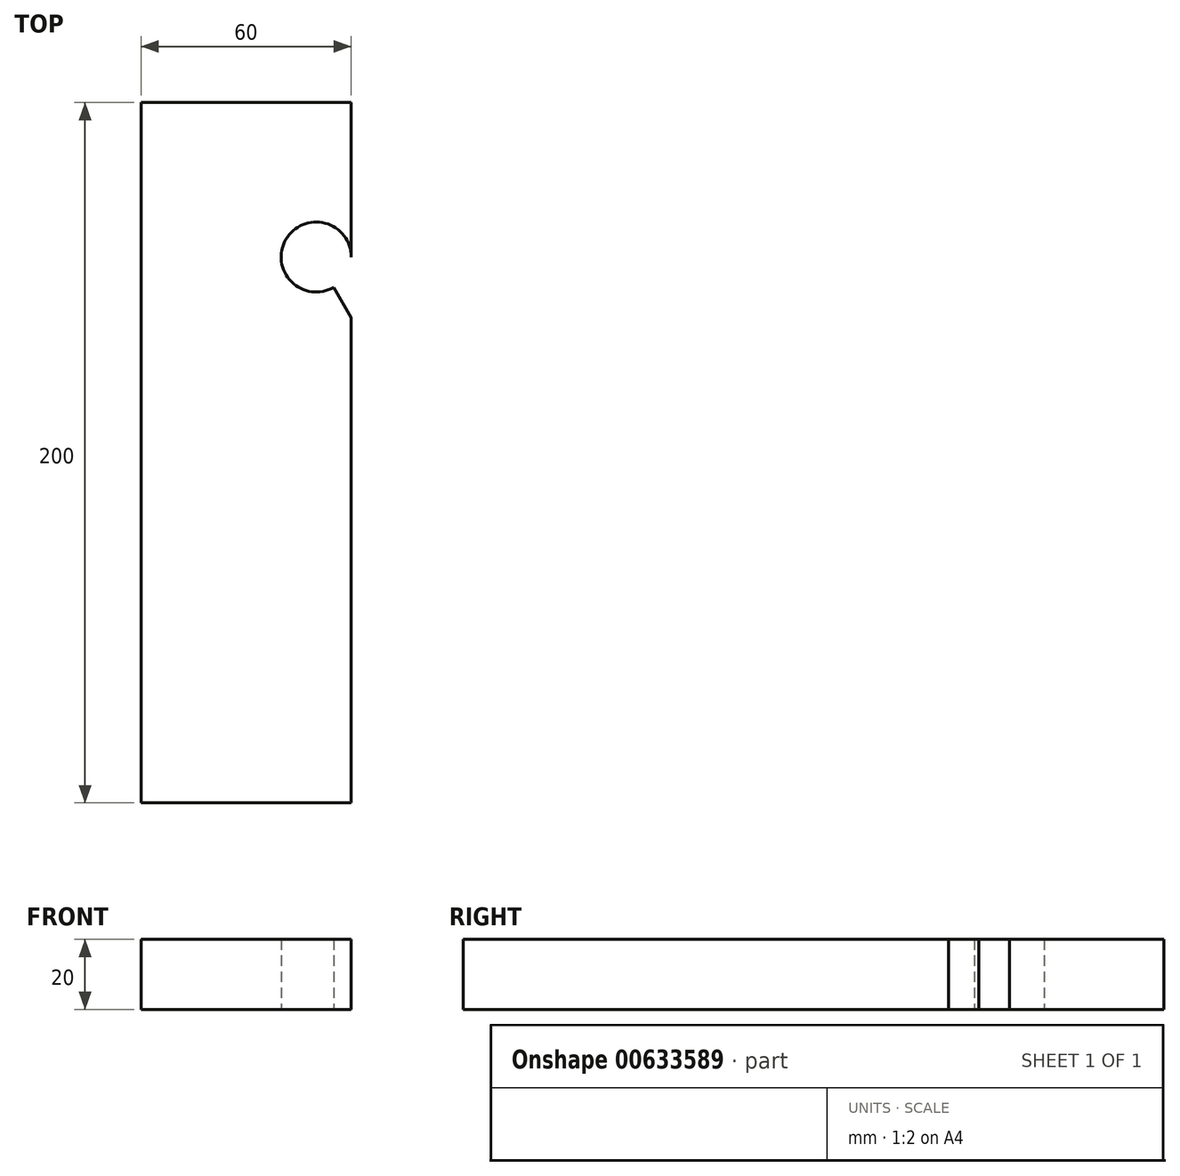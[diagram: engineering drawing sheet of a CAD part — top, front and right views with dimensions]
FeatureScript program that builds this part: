
annotation { "Feature Type Name" : "Feature", "Feature Type Description" : "" }
export const myFeature = defineFeature(function(context is Context, id is Id, definition is map)
    precondition{}
    {
        {
            var Q0;
            Q0=qCreatedBy(makeId("Top.planeOp"),FACE);
            var sketch = newSketch(context, id + "F0", { "sketchPlane" : qUnion([Q0])});
            skLineSegment(sketch, "E0", {"start": v(-30, 17.32) * mm, "end": v(30, 17.32) * mm});
            skLineSegment(sketch, "E1", {"start": v(30, 17.32) * mm, "end": v(0, -34.64) * mm, "construction": true});
            skLineSegment(sketch, "E2", {"start": v(0, -34.64) * mm, "end": v(-30, 17.32) * mm, "construction": true});
            skCircle(sketch, "E3", {"center": v(0, 0) * mm, "radius": 34.64 * mm, "construction": true});
            skLineSegment(sketch, "E4.bottom", {"start": v(-30, 217.32) * mm, "end": v(30, 217.32) * mm});
            skLineSegment(sketch, "E4.left", {"start": v(-30, 217.32) * mm, "end": v(-30, 17.32) * mm});
            skLineSegment(sketch, "E4.right", {"start": v(30, 217.32) * mm, "end": v(30, 17.32) * mm});
            skPoint(sketch, "E4.middle", {"position": v(0, 117.32) * mm});
            skLineSegment(sketch, "E5.bottom", {"start": v(-30, 217.32) * mm, "end": v(30, 217.32) * mm, "construction": true});
            skLineSegment(sketch, "E5.top", {"start": v(-30, 237.32) * mm, "end": v(30, 237.32) * mm, "construction": true});
            skLineSegment(sketch, "E5.left", {"start": v(-30, 217.32) * mm, "end": v(-30, 237.32) * mm, "construction": true});
            skLineSegment(sketch, "E5.right", {"start": v(30, 217.32) * mm, "end": v(30, 237.32) * mm, "construction": true});
            skPoint(sketch, "E5.middle", {"position": v(0, 227.32) * mm});
            skCircle(sketch, "E6", {"center": v(0, 0) * mm, "radius": 219.38 * mm, "construction": true});
            skLineSegment(sketch, "E7", {"start": v(-30, 203.82) * mm, "end": v(30, 203.82) * mm, "construction": true});
            skCircle(sketch, "E8", {"center": v(0, 0) * mm, "radius": 150 * mm, "construction": true});
            skLineSegment(sketch, "E9", {"start": v(-30, 17.32) * mm, "end": v(-203.2, -82.68) * mm, "construction": true});
            skLineSegment(sketch, "E10", {"start": v(-203.2, -82.68) * mm, "end": v(-173.2, -134.64) * mm, "construction": true});
            skLineSegment(sketch, "E11", {"start": v(-173.2, -134.64) * mm, "end": v(0, -34.64) * mm, "construction": true});
            skLineSegment(sketch, "E12", {"start": v(0, -34.64) * mm, "end": v(173.2, -134.64) * mm, "construction": true});
            skLineSegment(sketch, "E13", {"start": v(173.2, -134.64) * mm, "end": v(203.2, -82.68) * mm, "construction": true});
            skLineSegment(sketch, "E14", {"start": v(203.2, -82.68) * mm, "end": v(30, 17.32) * mm, "construction": true});
            skLineSegment(sketch, "E15", {"start": v(-30, 217.32) * mm, "end": v(-203.2, -82.68) * mm, "construction": true});
            skLineSegment(sketch, "E16", {"start": v(-173.2, -134.64) * mm, "end": v(173.2, -134.64) * mm, "construction": true});
            skLineSegment(sketch, "E17", {"start": v(203.2, -82.68) * mm, "end": v(30, 217.32) * mm, "construction": true});
            skLineSegment(sketch, "E18.bottom", {"start": v(-220.53, 237.32) * mm, "end": v(220.53, 237.32) * mm, "construction": true});
            skLineSegment(sketch, "E18.top", {"start": v(-220.53, -144.64) * mm, "end": v(220.53, -144.64) * mm, "construction": true});
            skLineSegment(sketch, "E18.left", {"start": v(-220.53, 237.32) * mm, "end": v(-220.53, -144.64) * mm, "construction": true});
            skLineSegment(sketch, "E18.right", {"start": v(220.53, 237.32) * mm, "end": v(220.53, -144.64) * mm, "construction": true});
            skLineSegment(sketch, "E19", {"start": v(173.2, -134.64) * mm, "end": v(190.53, -144.64) * mm, "construction": true});
            skLineSegment(sketch, "E20", {"start": v(190.53, -144.64) * mm, "end": v(220.53, -92.68) * mm, "construction": true});
            skLineSegment(sketch, "E21", {"start": v(220.53, -92.68) * mm, "end": v(203.2, -82.68) * mm, "construction": true});
            skLineSegment(sketch, "E22", {"start": v(-220.53, -92.68) * mm, "end": v(-190.53, -144.64) * mm, "construction": true});
            skLineSegment(sketch, "E23", {"start": v(-190.53, -144.64) * mm, "end": v(-173.2, -134.64) * mm, "construction": true});
            skLineSegment(sketch, "E24", {"start": v(-220.53, -92.68) * mm, "end": v(-203.2, -82.68) * mm, "construction": true});
            skLineSegment(sketch, "E25", {"start": v(0, 217.32) * mm, "end": v(-188.2, -108.66) * mm, "construction": true});
            skLineSegment(sketch, "E26", {"start": v(-188.2, -108.66) * mm, "end": v(188.2, -108.66) * mm, "construction": true});
            skLineSegment(sketch, "E27", {"start": v(188.2, -108.66) * mm, "end": v(0, 217.32) * mm, "construction": true});
            skCircle(sketch, "E28", {"center": v(0, 150) * mm, "radius": 27 * mm, "construction": true});
            skLineSegment(sketch, "E29", {"start": v(-54, 169.84) * mm, "end": v(-54, 112.13) * mm, "construction": true});
            skLineSegment(sketch, "E30", {"start": v(-68.75, 177.32) * mm, "end": v(-11.19, 177.32) * mm, "construction": true});
            skLineSegment(sketch, "E31", {"start": v(20, 173.2) * mm, "end": v(160, -69.28) * mm});
            skCircle(sketch, "E32", {"center": v(20, 173.2) * mm, "radius": 10 * mm});
            skCircle(sketch, "E33", {"center": v(160, -69.28) * mm, "radius": 10 * mm});
            skLineSegment(sketch, "E34", {"start": v(94.1, 54.33) * mm, "end": v(30, 17.32) * mm, "construction": true});
            skPoint(sketch, "E35", {"position": v(90, 51.96) * mm});
            skSolve(sketch);
        }
        {
            var Q0;
            Q0=makeQuery(id+"F0.imprint","IMPRINT",FACE,{"disambiguationData":[TD([[makeQuery(id+"F0.imprint","IMPRINT",EDGE,{"derivedFrom":sQuery(id+"F0.wireOp",EDGE,"E4.bottom")}),-1.0]])]});
            extrude(context, id + "F1", {"entities" : qUnion([Q0]), "depth" : 20 * mm, "offsetDistance" : 25 * mm});
        }
    });
